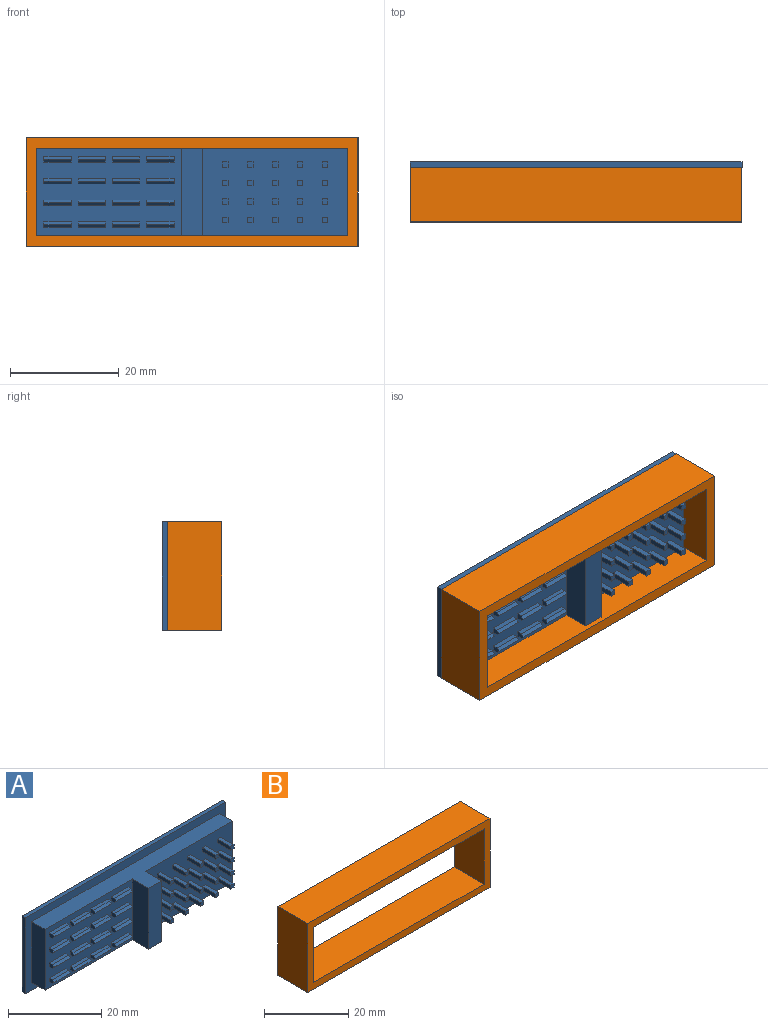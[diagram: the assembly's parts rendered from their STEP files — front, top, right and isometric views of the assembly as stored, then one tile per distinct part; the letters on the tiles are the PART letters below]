
ASSEMBLY  parts=2 mates=1
PART A: 211 faces, bbox 61x10x20 mm
  f0: plane 16x4mm, normal (0,-1,0), area 64mm2, adj f1,f3,f203,f204
  f1: plane 16x5mm, normal (1,0,0), area 80mm2, adj f0,f2,f203,f204
  f2: plane 26.5x16mm, normal (0,-1,0), area 404mm2, adj f1,f101,f102,f103,f104,f106,f107,f108
  f3: plane 16x5mm, normal (-1,0,0), area 80mm2, adj f0,f4,f203,f204
  f4: plane 26.5x16mm, normal (0,-1,0), area 344mm2, adj f3,f5,f6,f7,f8,f9,f10,f11
  f5: plane 5x0.9mm, normal (0,0,1), area 4.5mm2, adj f4,f6,f8,f100
  f6: plane 1.4x1mm, normal (-1,0,0), area 1.1mm2, adj f4,f5,f7,f99,f100
  f7: plane 5x0.9mm, normal (0,0,-1), area 4.5mm2, adj f4,f6,f8,f99
  f8: plane 1.4x1mm, normal (1,0,0), area 1.2mm2, adj f4,f5,f7,f99,f100
  f9: plane 5x0.9mm, normal (0,0,1), area 4.5mm2, adj f4,f10,f12,f98
  f10: plane 1.4x1mm, normal (-1,0,0), area 1.1mm2, adj f4,f9,f11,f97,f98
  f11: plane 5x0.9mm, normal (0,0,-1), area 4.5mm2, adj f4,f10,f12,f97
  f12: plane 1.4x1mm, normal (1,0,0), area 1.2mm2, adj f4,f9,f11,f97,f98
  f13: plane 5x0.9mm, normal (0,0,1), area 4.5mm2, adj f4,f14,f16,f96
  f14: plane 1.4x1mm, normal (-1,0,0), area 1.1mm2, adj f4,f13,f15,f95,f96
  f15: plane 5x0.9mm, normal (0,0,-1), area 4.5mm2, adj f4,f14,f16,f95
  f16: plane 1.4x1mm, normal (1,0,0), area 1.2mm2, adj f4,f13,f15,f95,f96
  f17: plane 5x0.9mm, normal (0,0,1), area 4.5mm2, adj f4,f18,f20,f94
  f18: plane 1.4x1mm, normal (-1,0,0), area 1.1mm2, adj f4,f17,f19,f93,f94
  f19: plane 5x0.9mm, normal (0,0,-1), area 4.5mm2, adj f4,f18,f20,f93
  f20: plane 1.4x1mm, normal (1,0,0), area 1.2mm2, adj f4,f17,f19,f93,f94
  f21: plane 5x0.9mm, normal (0,0,1), area 4.5mm2, adj f4,f22,f24,f91
  f22: plane 1.4x1mm, normal (-1,0,0), area 1.1mm2, adj f4,f21,f23,f91,f92
  f23: plane 5x0.9mm, normal (0,0,-1), area 4.5mm2, adj f4,f22,f24,f92
  f24: plane 1.4x1mm, normal (1,0,0), area 1.1mm2, adj f4,f21,f23,f91,f92
  f25: plane 5x0.9mm, normal (0,0,1), area 4.5mm2, adj f4,f26,f28,f90
  f26: plane 1.4x1mm, normal (-1,0,0), area 1.1mm2, adj f4,f25,f27,f89,f90
  f27: plane 5x0.9mm, normal (0,0,-1), area 4.5mm2, adj f4,f26,f28,f89
  f28: plane 1.4x1mm, normal (1,0,0), area 1.1mm2, adj f4,f25,f27,f89,f90
  f29: plane 5x0.9mm, normal (0,0,1), area 4.5mm2, adj f4,f30,f32,f87
  f30: plane 1.4x1mm, normal (-1,0,0), area 1.1mm2, adj f4,f29,f31,f87,f88
  f31: plane 5x0.9mm, normal (0,0,-1), area 4.5mm2, adj f4,f30,f32,f88
  f32: plane 1.4x1mm, normal (1,0,0), area 1.1mm2, adj f4,f29,f31,f87,f88
  f33: plane 5x0.9mm, normal (0,0,1), area 4.5mm2, adj f4,f34,f36,f86
  f34: plane 1.4x1mm, normal (-1,0,0), area 1.1mm2, adj f4,f33,f35,f85,f86
  f35: plane 5x0.9mm, normal (0,0,-1), area 4.5mm2, adj f4,f34,f36,f85
  f36: plane 1.4x1mm, normal (1,0,0), area 1.1mm2, adj f4,f33,f35,f85,f86
  f37: plane 5x0.9mm, normal (0,0,1), area 4.5mm2, adj f4,f38,f40,f78
  f38: plane 1.4x1mm, normal (-1,0,0), area 1.1mm2, adj f4,f37,f39,f77,f78
  f39: plane 5x0.9mm, normal (0,0,-1), area 4.5mm2, adj f4,f38,f40,f77
  f40: plane 1.4x1mm, normal (1,0,0), area 1.1mm2, adj f4,f37,f39,f77,f78
  f41: plane 5x0.9mm, normal (0,0,1), area 4.5mm2, adj f4,f42,f44,f80
  f42: plane 1.4x1mm, normal (-1,0,0), area 1.1mm2, adj f4,f41,f43,f79,f80
  f43: plane 5x0.9mm, normal (0,0,-1), area 4.5mm2, adj f4,f42,f44,f79
  f44: plane 1.4x1mm, normal (1,0,0), area 1.1mm2, adj f4,f41,f43,f79,f80
  f45: plane 5x0.9mm, normal (0,0,1), area 4.5mm2, adj f4,f46,f48,f81
  f46: plane 1.4x1mm, normal (-1,0,0), area 1.1mm2, adj f4,f45,f47,f81,f82
  f47: plane 5x0.9mm, normal (0,0,-1), area 4.5mm2, adj f4,f46,f48,f82
  f48: plane 1.4x1mm, normal (1,0,0), area 1.1mm2, adj f4,f45,f47,f81,f82
  f49: plane 5x0.9mm, normal (0,0,1), area 4.5mm2, adj f4,f50,f52,f84
  f50: plane 1.4x1mm, normal (-1,0,0), area 1.1mm2, adj f4,f49,f51,f83,f84
  f51: plane 5x0.9mm, normal (0,0,-1), area 4.5mm2, adj f4,f50,f52,f83
  f52: plane 1.4x1mm, normal (1,0,0), area 1.1mm2, adj f4,f49,f51,f83,f84
  f53: plane 5x0.9mm, normal (0,0,1), area 4.5mm2, adj f4,f54,f56,f76
  f54: plane 1.4x1mm, normal (-1,0,0), area 1.1mm2, adj f4,f53,f55,f75,f76
  f55: plane 5x0.9mm, normal (0,0,-1), area 4.5mm2, adj f4,f54,f56,f75
  f56: plane 1.4x1mm, normal (1,0,0), area 1.1mm2, adj f4,f53,f55,f75,f76
  f57: plane 5x0.9mm, normal (0,0,1), area 4.5mm2, adj f4,f58,f60,f73
  f58: plane 1.4x1mm, normal (-1,0,0), area 1.1mm2, adj f4,f57,f59,f73,f74
  f59: plane 5x0.9mm, normal (0,0,-1), area 4.5mm2, adj f4,f58,f60,f74
  f60: plane 1.4x1mm, normal (1,0,0), area 1.1mm2, adj f4,f57,f59,f73,f74
  f61: plane 5x0.9mm, normal (0,0,1), area 4.5mm2, adj f4,f62,f64,f72
  f62: plane 1.4x1mm, normal (-1,0,0), area 1.1mm2, adj f4,f61,f63,f71,f72
  f63: plane 5x0.9mm, normal (0,0,-1), area 4.5mm2, adj f4,f62,f64,f71
  f64: plane 1.4x1mm, normal (1,0,0), area 1.1mm2, adj f4,f61,f63,f71,f72
  f65: plane 5x0.9mm, normal (0,0,1), area 4.5mm2, adj f4,f66,f68,f69
  f66: plane 1.4x1mm, normal (-1,0,0), area 1.1mm2, adj f4,f65,f67,f69,f70
  f67: plane 5x0.9mm, normal (0,0,-1), area 4.5mm2, adj f4,f66,f68,f70
  f68: plane 1.4x1mm, normal (1,0,0), area 1.1mm2, adj f4,f65,f67,f69,f70
  f69: plane 5x0.5mm, normal (0,-0.71,0.71), area 3.5mm2, adj f65,f66,f68,f70
  f70: plane 5x0.5mm, normal (0,-0.71,-0.71), area 3.5mm2, adj f66,f67,f68,f69
  f71: plane 5x0.5mm, normal (0,-0.71,-0.71), area 3.5mm2, adj f62,f63,f64,f72
  f72: plane 5x0.5mm, normal (0,-0.71,0.71), area 3.5mm2, adj f61,f62,f64,f71
  f73: plane 5x0.5mm, normal (0,-0.71,0.71), area 3.5mm2, adj f57,f58,f60,f74
  f74: plane 5x0.5mm, normal (0,-0.71,-0.71), area 3.5mm2, adj f58,f59,f60,f73
  f75: plane 5x0.5mm, normal (0,-0.71,-0.71), area 3.5mm2, adj f54,f55,f56,f76
  f76: plane 5x0.5mm, normal (0,-0.71,0.71), area 3.5mm2, adj f53,f54,f56,f75
  f77: plane 5x0.5mm, normal (0,-0.71,-0.71), area 3.5mm2, adj f38,f39,f40,f78
  f78: plane 5x0.5mm, normal (0,-0.71,0.71), area 3.5mm2, adj f37,f38,f40,f77
  f79: plane 5x0.5mm, normal (0,-0.71,-0.71), area 3.5mm2, adj f42,f43,f44,f80
  f80: plane 5x0.5mm, normal (0,-0.71,0.71), area 3.5mm2, adj f41,f42,f44,f79
  f81: plane 5x0.5mm, normal (0,-0.71,0.71), area 3.5mm2, adj f45,f46,f48,f82
  f82: plane 5x0.5mm, normal (0,-0.71,-0.71), area 3.5mm2, adj f46,f47,f48,f81
  f83: plane 5x0.5mm, normal (0,-0.71,-0.71), area 3.5mm2, adj f50,f51,f52,f84
  f84: plane 5x0.5mm, normal (0,-0.71,0.71), area 3.5mm2, adj f49,f50,f52,f83
  f85: plane 5x0.5mm, normal (0,-0.71,-0.71), area 3.5mm2, adj f34,f35,f36,f86
  f86: plane 5x0.5mm, normal (0,-0.71,0.71), area 3.5mm2, adj f33,f34,f36,f85
  f87: plane 5x0.5mm, normal (0,-0.71,0.71), area 3.5mm2, adj f29,f30,f32,f88
  f88: plane 5x0.5mm, normal (0,-0.71,-0.71), area 3.5mm2, adj f30,f31,f32,f87
  f89: plane 5x0.5mm, normal (0,-0.71,-0.71), area 3.5mm2, adj f26,f27,f28,f90
  f90: plane 5x0.5mm, normal (0,-0.71,0.71), area 3.5mm2, adj f25,f26,f28,f89
  f91: plane 5x0.5mm, normal (0,-0.71,0.71), area 3.5mm2, adj f21,f22,f24,f92
  f92: plane 5x0.5mm, normal (0,-0.71,-0.71), area 3.5mm2, adj f22,f23,f24,f91
  f93: plane 5x0.5mm, normal (0,-0.71,-0.71), area 3.5mm2, adj f18,f19,f20,f94
  f94: plane 5x0.5mm, normal (0,-0.71,0.71), area 3.5mm2, adj f17,f18,f20,f93
  f95: plane 5x0.5mm, normal (0,-0.71,-0.71), area 3.5mm2, adj f14,f15,f16,f96
  f96: plane 5x0.5mm, normal (0,-0.71,0.71), area 3.5mm2, adj f13,f14,f16,f95
  f97: plane 5x0.5mm, normal (0,-0.71,-0.71), area 3.5mm2, adj f10,f11,f12,f98
  f98: plane 5x0.5mm, normal (0,-0.71,0.71), area 3.5mm2, adj f9,f10,f12,f97
  f99: plane 5x0.5mm, normal (0,-0.71,-0.71), area 3.5mm2, adj f6,f7,f8,f100
  f100: plane 5x0.5mm, normal (0,-0.71,0.71), area 3.5mm2, adj f5,f6,f8,f99
  f101: plane 4x1mm, normal (0,0,1), area 4mm2, adj f2,f102,f104,f105
  f102: plane 4x1mm, normal (-1,0,0), area 4mm2, adj f2,f101,f103,f105
  f103: plane 4x1mm, normal (0,0,-1), area 4mm2, adj f2,f102,f104,f105
  f104: plane 4x1mm, normal (1,0,0), area 4mm2, adj f2,f101,f103,f105
  f105: plane 1x1mm, normal (0,-1,0), area 1mm2, adj f101,f102,f103,f104
  f106: plane 4x1mm, normal (0,0,1), area 4mm2, adj f2,f107,f109,f110
  f107: plane 4x1mm, normal (-1,0,0), area 4mm2, adj f2,f106,f108,f110
  f108: plane 4x1mm, normal (0,0,-1), area 4mm2, adj f2,f107,f109,f110
  f109: plane 4x1mm, normal (1,0,0), area 4mm2, adj f2,f106,f108,f110
  f110: plane 1x1mm, normal (0,-1,0), area 1mm2, adj f106,f107,f108,f109
  f111: plane 4x1mm, normal (0,0,1), area 4mm2, adj f2,f112,f114,f115
  f112: plane 4x1mm, normal (-1,0,0), area 4mm2, adj f2,f111,f113,f115
  f113: plane 4x1mm, normal (0,0,-1), area 4mm2, adj f2,f112,f114,f115
  f114: plane 4x1mm, normal (1,0,0), area 4mm2, adj f2,f111,f113,f115
  f115: plane 1x1mm, normal (0,-1,0), area 1mm2, adj f111,f112,f113,f114
  f116: plane 4x1mm, normal (0,0,1), area 4mm2, adj f2,f117,f119,f120
  f117: plane 4x1mm, normal (-1,0,0), area 4mm2, adj f2,f116,f118,f120
  f118: plane 4x1mm, normal (0,0,-1), area 4mm2, adj f2,f117,f119,f120
  f119: plane 4x1mm, normal (1,0,0), area 4mm2, adj f2,f116,f118,f120
  f120: plane 1x1mm, normal (0,-1,0), area 1mm2, adj f116,f117,f118,f119
  f121: plane 4x1mm, normal (0,0,1), area 4mm2, adj f2,f122,f124,f125
  f122: plane 4x1mm, normal (-1,0,0), area 4mm2, adj f2,f121,f123,f125
  f123: plane 4x1mm, normal (0,0,-1), area 4mm2, adj f2,f122,f124,f125
  f124: plane 4x1mm, normal (1,0,0), area 4mm2, adj f2,f121,f123,f125
  f125: plane 1x1mm, normal (0,-1,0), area 1mm2, adj f121,f122,f123,f124
  f126: plane 4x1mm, normal (0,0,1), area 4mm2, adj f2,f127,f129,f130
  f127: plane 4x1mm, normal (-1,0,0), area 4mm2, adj f2,f126,f128,f130
  f128: plane 4x1mm, normal (0,0,-1), area 4mm2, adj f2,f127,f129,f130
  f129: plane 4x1mm, normal (1,0,0), area 4mm2, adj f2,f126,f128,f130
  f130: plane 1x1mm, normal (0,-1,0), area 1mm2, adj f126,f127,f128,f129
  f131: plane 4x1mm, normal (0,0,1), area 4mm2, adj f2,f132,f134,f135
  f132: plane 4x1mm, normal (-1,0,0), area 4mm2, adj f2,f131,f133,f135
  f133: plane 4x1mm, normal (0,0,-1), area 4mm2, adj f2,f132,f134,f135
  f134: plane 4x1mm, normal (1,0,0), area 4mm2, adj f2,f131,f133,f135
  f135: plane 1x1mm, normal (0,-1,0), area 1mm2, adj f131,f132,f133,f134
  f136: plane 4x1mm, normal (0,0,1), area 4mm2, adj f2,f137,f139,f140
  f137: plane 4x1mm, normal (-1,0,0), area 4mm2, adj f2,f136,f138,f140
  f138: plane 4x1mm, normal (0,0,-1), area 4mm2, adj f2,f137,f139,f140
  f139: plane 4x1mm, normal (1,0,0), area 4mm2, adj f2,f136,f138,f140
  f140: plane 1x1mm, normal (0,-1,0), area 1mm2, adj f136,f137,f138,f139
  f141: plane 4x1mm, normal (0,0,1), area 4mm2, adj f2,f142,f144,f145
  f142: plane 4x1mm, normal (-1,0,0), area 4mm2, adj f2,f141,f143,f145
  f143: plane 4x1mm, normal (0,0,-1), area 4mm2, adj f2,f142,f144,f145
  f144: plane 4x1mm, normal (1,0,0), area 4mm2, adj f2,f141,f143,f145
  f145: plane 1x1mm, normal (0,-1,0), area 1mm2, adj f141,f142,f143,f144
  f146: plane 4x1mm, normal (0,0,1), area 4mm2, adj f2,f147,f149,f150
  f147: plane 4x1mm, normal (-1,0,0), area 4mm2, adj f2,f146,f148,f150
  f148: plane 4x1mm, normal (0,0,-1), area 4mm2, adj f2,f147,f149,f150
  f149: plane 4x1mm, normal (1,0,0), area 4mm2, adj f2,f146,f148,f150
  f150: plane 1x1mm, normal (0,-1,0), area 1mm2, adj f146,f147,f148,f149
  f151: plane 4x1mm, normal (0,0,1), area 4mm2, adj f2,f152,f154,f155
  f152: plane 4x1mm, normal (-1,0,0), area 4mm2, adj f2,f151,f153,f155
  f153: plane 4x1mm, normal (0,0,-1), area 4mm2, adj f2,f152,f154,f155
  f154: plane 4x1mm, normal (1,0,0), area 4mm2, adj f2,f151,f153,f155
  f155: plane 1x1mm, normal (0,-1,0), area 1mm2, adj f151,f152,f153,f154
  f156: plane 4x1mm, normal (0,0,1), area 4mm2, adj f2,f157,f159,f160
  f157: plane 4x1mm, normal (-1,0,0), area 4mm2, adj f2,f156,f158,f160
  f158: plane 4x1mm, normal (0,0,-1), area 4mm2, adj f2,f157,f159,f160
  f159: plane 4x1mm, normal (1,0,0), area 4mm2, adj f2,f156,f158,f160
  f160: plane 1x1mm, normal (0,-1,0), area 1mm2, adj f156,f157,f158,f159
  f161: plane 4x1mm, normal (0,0,1), area 4mm2, adj f2,f162,f164,f165
  f162: plane 4x1mm, normal (-1,0,0), area 4mm2, adj f2,f161,f163,f165
  f163: plane 4x1mm, normal (0,0,-1), area 4mm2, adj f2,f162,f164,f165
  f164: plane 4x1mm, normal (1,0,0), area 4mm2, adj f2,f161,f163,f165
  f165: plane 1x1mm, normal (0,-1,0), area 1mm2, adj f161,f162,f163,f164
  f166: plane 4x1mm, normal (0,0,1), area 4mm2, adj f2,f167,f169,f170
  f167: plane 4x1mm, normal (-1,0,0), area 4mm2, adj f2,f166,f168,f170
  f168: plane 4x1mm, normal (0,0,-1), area 4mm2, adj f2,f167,f169,f170
  f169: plane 4x1mm, normal (1,0,0), area 4mm2, adj f2,f166,f168,f170
  f170: plane 1x1mm, normal (0,-1,0), area 1mm2, adj f166,f167,f168,f169
  f171: plane 4x1mm, normal (0,0,1), area 4mm2, adj f2,f172,f174,f175
  f172: plane 4x1mm, normal (-1,0,0), area 4mm2, adj f2,f171,f173,f175
  f173: plane 4x1mm, normal (0,0,-1), area 4mm2, adj f2,f172,f174,f175
  f174: plane 4x1mm, normal (1,0,0), area 4mm2, adj f2,f171,f173,f175
  f175: plane 1x1mm, normal (0,-1,0), area 1mm2, adj f171,f172,f173,f174
  f176: plane 4x1mm, normal (0,0,1), area 4mm2, adj f2,f177,f179,f180
  f177: plane 4x1mm, normal (-1,0,0), area 4mm2, adj f2,f176,f178,f180
  f178: plane 4x1mm, normal (0,0,-1), area 4mm2, adj f2,f177,f179,f180
  f179: plane 4x1mm, normal (1,0,0), area 4mm2, adj f2,f176,f178,f180
  f180: plane 1x1mm, normal (0,-1,0), area 1mm2, adj f176,f177,f178,f179
  f181: plane 4x1mm, normal (0,0,1), area 4mm2, adj f2,f182,f184,f185
  f182: plane 4x1mm, normal (-1,0,0), area 4mm2, adj f2,f181,f183,f185
  f183: plane 4x1mm, normal (0,0,-1), area 4mm2, adj f2,f182,f184,f185
  f184: plane 4x1mm, normal (1,0,0), area 4mm2, adj f2,f181,f183,f185
  f185: plane 1x1mm, normal (0,-1,0), area 1mm2, adj f181,f182,f183,f184
  f186: plane 4x1mm, normal (0,0,1), area 4mm2, adj f2,f187,f189,f190
  f187: plane 4x1mm, normal (-1,0,0), area 4mm2, adj f2,f186,f188,f190
  f188: plane 4x1mm, normal (0,0,-1), area 4mm2, adj f2,f187,f189,f190
  f189: plane 4x1mm, normal (1,0,0), area 4mm2, adj f2,f186,f188,f190
  f190: plane 1x1mm, normal (0,-1,0), area 1mm2, adj f186,f187,f188,f189
  f191: plane 4x1mm, normal (0,0,1), area 4mm2, adj f2,f192,f194,f195
  f192: plane 4x1mm, normal (-1,0,0), area 4mm2, adj f2,f191,f193,f195
  f193: plane 4x1mm, normal (0,0,-1), area 4mm2, adj f2,f192,f194,f195
  f194: plane 4x1mm, normal (1,0,0), area 4mm2, adj f2,f191,f193,f195
  f195: plane 1x1mm, normal (0,-1,0), area 1mm2, adj f191,f192,f193,f194
  f196: plane 4x1mm, normal (0,0,1), area 4mm2, adj f2,f197,f199,f200
  f197: plane 4x1mm, normal (-1,0,0), area 4mm2, adj f2,f196,f198,f200
  f198: plane 4x1mm, normal (0,0,-1), area 4mm2, adj f2,f197,f199,f200
  f199: plane 4x1mm, normal (1,0,0), area 4mm2, adj f2,f196,f198,f200
  f200: plane 1x1mm, normal (0,-1,0), area 1mm2, adj f196,f197,f198,f199
  f201: plane 16x4mm, normal (1,0,0), area 64mm2, adj f2,f203,f204,f205
  f202: plane 16x4mm, normal (-1,0,0), area 64mm2, adj f4,f203,f204,f205
  f203: plane 57x9mm, normal (0,0,1), area 248mm2, adj f0,f1,f2,f3,f4,f201,f202,f205
  f204: plane 57x9mm, normal (0,0,-1), area 248mm2, adj f0,f1,f2,f3,f4,f201,f202,f205
  f205: plane 61x20mm, normal (0,-1,0), area 308mm2, adj f201,f202,f203,f204,f207,f208,f209,f210
  f206: plane 61x20mm, normal (0,1,0), area 1220mm2, adj f207,f208,f209,f210
  f207: plane 20x1mm, normal (-1,0,0), area 20mm2, adj f205,f206,f208,f210
  f208: plane 61x1mm, normal (0,0,1), area 61mm2, adj f205,f206,f207,f209
  f209: plane 20x1mm, normal (1,0,0), area 20mm2, adj f205,f206,f208,f210
  f210: plane 61x1mm, normal (0,0,-1), area 61mm2, adj f205,f206,f207,f209
PART B: 10 faces, bbox 61x10x20 mm
  f0: plane 61x10mm, normal (0,0,1), area 610mm2, adj f1,f7,f8,f9
  f1: plane 20x10mm, normal (-1,0,0), area 200mm2, adj f0,f2,f8,f9
  f2: plane 61x10mm, normal (0,0,-1), area 610mm2, adj f1,f7,f8,f9
  f3: plane 16x10mm, normal (1,0,0), area 160mm2, adj f4,f6,f8,f9
  f4: plane 57x10mm, normal (0,0,-1), area 570mm2, adj f3,f5,f8,f9
  f5: plane 16x10mm, normal (-1,0,0), area 160mm2, adj f4,f6,f8,f9
  f6: plane 57x10mm, normal (0,0,1), area 570mm2, adj f3,f5,f8,f9
  f7: plane 20x10mm, normal (1,0,0), area 200mm2, adj f0,f2,f8,f9
  f8: plane 61x20mm, normal (0,-1,0), area 308mm2, adj f0,f1,f2,f3,f4,f5,f6,f7
  f9: plane 61x20mm, normal (0,1,0), area 308mm2, adj f0,f1,f2,f3,f4,f5,f6,f7
PLACE A t=(1.36,-9.76,6.17)mm
PLACE B t=(-0.42,-5.76,12.92)mm
MATE fastened A.f205 <-> B.f9  axis (0,-1,0) through (1.36,-5.76,6.17)mm
